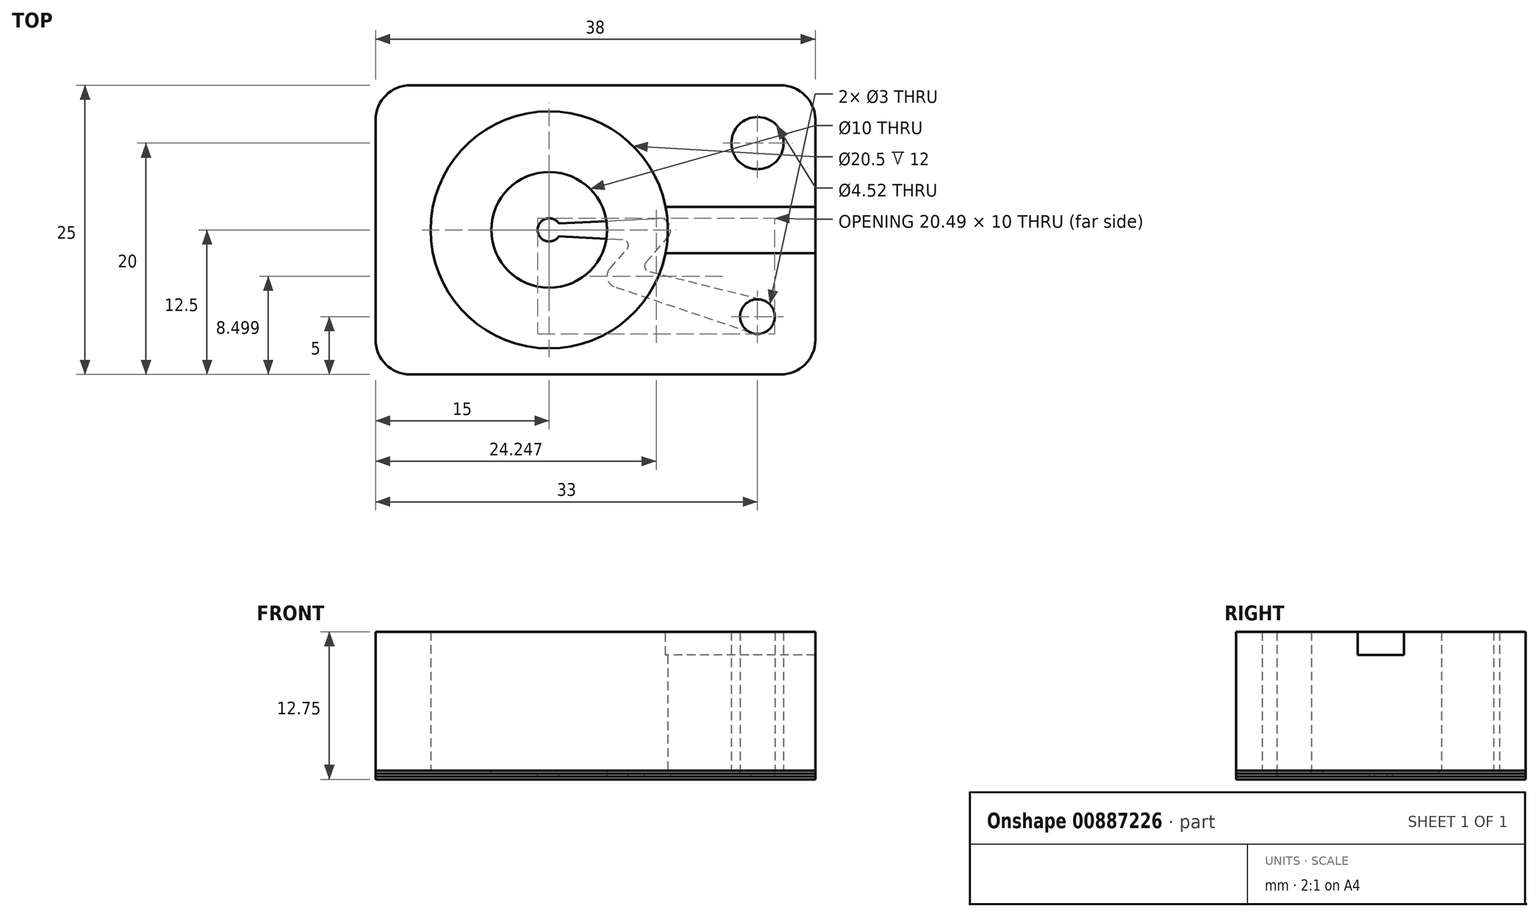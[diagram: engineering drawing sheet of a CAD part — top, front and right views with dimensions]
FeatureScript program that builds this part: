
annotation { "Feature Type Name" : "Feature", "Feature Type Description" : "" }
export const myFeature = defineFeature(function(context is Context, id is Id, definition is map)
    precondition{}
    {
        {
            var Q0;
            Q0=qCreatedBy(makeId("Top.planeOp"),FACE);
            var sketch = newSketch(context, id + "F0", { "sketchPlane" : qUnion([Q0])});
            skLineSegment(sketch, "E0.bottom", {"start": v(16, -12.5) * mm, "end": v(-16, -12.5) * mm});
            skLineSegment(sketch, "E0.top", {"start": v(16, 12.5) * mm, "end": v(-16, 12.5) * mm});
            skLineSegment(sketch, "E0.left", {"start": v(19, -9.5) * mm, "end": v(19, 9.5) * mm});
            skLineSegment(sketch, "E0.right", {"start": v(-19, -9.5) * mm, "end": v(-19, 9.5) * mm});
            skPoint(sketch, "E0.middle", {"position": v(0, 0) * mm});
            skCircle(sketch, "E1", {"center": v(-4, 0) * mm, "radius": 10.25 * mm});
            skLineSegment(sketch, "E2", {"start": v(14, 12.5) * mm, "end": v(14, -12.5) * mm, "construction": true});
            skCircle(sketch, "E3", {"center": v(14, -7.5) * mm, "radius": 1.5 * mm});
            skCircle(sketch, "E4", {"center": v(14, 7.5) * mm, "radius": 2.26 * mm});
            skPoint(sketch, "E5.visualSharp", {"position": v(19, 12.5) * mm});
            skArc(sketch, "E5.filletArc", {"start": v(19, 9.5) * mm, "mid": v(18.12, 11.62) * mm, "end": v(16, 12.5) * mm});
            skPoint(sketch, "E6.visualSharp", {"position": v(-19, 12.5) * mm});
            skArc(sketch, "E6.filletArc", {"start": v(-16, 12.5) * mm, "mid": v(-18.12, 11.62) * mm, "end": v(-19, 9.5) * mm});
            skPoint(sketch, "E7.visualSharp", {"position": v(-19, -12.5) * mm});
            skArc(sketch, "E7.filletArc", {"start": v(-19, -9.5) * mm, "mid": v(-18.12, -11.62) * mm, "end": v(-16, -12.5) * mm});
            skPoint(sketch, "E8.visualSharp", {"position": v(19, -12.5) * mm});
            skArc(sketch, "E8.filletArc", {"start": v(16, -12.5) * mm, "mid": v(18.12, -11.62) * mm, "end": v(19, -9.5) * mm});
            skSolve(sketch);
        }
        {
            var Q0;
            Q0=makeQuery(id+"F0.imprint","IMPRINT",FACE,{"disambiguationData":[TD([[makeQuery(id+"F0.imprint","IMPRINT",EDGE,{"derivedFrom":sQuery(id+"F0.wireOp",EDGE,"E0.bottom")}),-1.0]])]});
            extrude(context, id + "F1", {"entities" : qUnion([Q0]), "depth" : 12 * mm, "offsetDistance" : 25 * mm});
        }
        {
            var Q0;
            Q0=makeQuery(id+"F1.opExtrude","CAP_FACE",FACE,{"disambiguationData":[OSD([sQuery(id+"F0.wireOp",EDGE,"E0.bottom"),sQuery(id+"F0.wireOp",EDGE,"E0.top"),sQuery(id+"F0.wireOp",EDGE,"E0.left"),sQuery(id+"F0.wireOp",EDGE,"E0.right"),sQuery(id+"F0.wireOp",EDGE,"E1"),sQuery(id+"F0.wireOp",EDGE,"E3"),sQuery(id+"F0.wireOp",EDGE,"E4"),sQuery(id+"F0.wireOp",EDGE,"E5.filletArc"),sQuery(id+"F0.wireOp",EDGE,"E6.filletArc"),sQuery(id+"F0.wireOp",EDGE,"E7.filletArc"),sQuery(id+"F0.wireOp",EDGE,"E8.filletArc")])],"isStart":false});
            var sketch = newSketch(context, id + "F2", { "sketchPlane" : qUnion([Q0])});
            skLineSegment(sketch, "E9.0", {"start": v(19, -2) * mm, "end": v(19, 2) * mm});
            skArc(sketch, "E10.0", {"start": v(6.05, -2) * mm, "mid": v(6.25, 0) * mm, "end": v(6.05, 2) * mm});
            skLineSegment(sketch, "E11.bottom", {"start": v(19, -2) * mm, "end": v(6.05, -2) * mm});
            skLineSegment(sketch, "E11.top", {"start": v(19, 2) * mm, "end": v(6.05, 2) * mm});
            skPoint(sketch, "E11.middle", {"position": v(13.13, 0) * mm});
            skPoint(sketch, "E12.orphan", {"position": v(22.63, 2) * mm});
            skPoint(sketch, "E13.orphan", {"position": v(22.63, -2) * mm});
            skPoint(sketch, "E14.orphan", {"position": v(19, -9.5) * mm});
            skPoint(sketch, "E11.right.start.orphan", {"position": v(3.62, -2) * mm});
            skPoint(sketch, "E15.orphan", {"position": v(3.62, 2) * mm});
            skPoint(sketch, "E16.orphan", {"position": v(19, 9.5) * mm});
            skSolve(sketch);
        }
        {
            var Q0;
            Q0=makeQuery(id+"F2.imprint","IMPRINT",FACE,{"disambiguationData":[TD([[makeQuery(id+"F2.imprint","IMPRINT",EDGE,{"derivedFrom":sQuery(id+"F2.wireOp",EDGE,"E9.0")}),1.0]])]});
            extrude(context, id + "F3", {"entities" : qUnion([Q0]), "operationType" : NewBodyOperationType.REMOVE, "oppositeDirection" : true, "depth" : 2 * mm, "offsetDistance" : 25 * mm});
        }
        {
            var Q0;
            Q0=makeQuery(id+"F1.opExtrude","CAP_FACE",FACE,{"disambiguationData":[OSD([sQuery(id+"F0.wireOp",EDGE,"E0.bottom"),sQuery(id+"F0.wireOp",EDGE,"E0.top"),sQuery(id+"F0.wireOp",EDGE,"E0.left"),sQuery(id+"F0.wireOp",EDGE,"E0.right"),sQuery(id+"F0.wireOp",EDGE,"E1"),sQuery(id+"F0.wireOp",EDGE,"E3"),sQuery(id+"F0.wireOp",EDGE,"E4"),sQuery(id+"F0.wireOp",EDGE,"E5.filletArc"),sQuery(id+"F0.wireOp",EDGE,"E6.filletArc"),sQuery(id+"F0.wireOp",EDGE,"E7.filletArc"),sQuery(id+"F0.wireOp",EDGE,"E8.filletArc")])],"isStart":true});
            var sketch = newSketch(context, id + "F4", { "sketchPlane" : qUnion([Q0])});
            skLineSegment(sketch, "E17.0", {"start": v(16, -12.5) * mm, "end": v(-16, -12.5) * mm});
            skArc(sketch, "E18.0", {"start": v(19, -9.5) * mm, "mid": v(18.12, -11.62) * mm, "end": v(16, -12.5) * mm});
            skLineSegment(sketch, "E19.0", {"start": v(19, 9.5) * mm, "end": v(19, -9.5) * mm});
            skArc(sketch, "E20.0", {"start": v(16, 12.5) * mm, "mid": v(18.12, 11.62) * mm, "end": v(19, 9.5) * mm});
            skLineSegment(sketch, "E21.0", {"start": v(16, 12.5) * mm, "end": v(-16, 12.5) * mm});
            skArc(sketch, "E22.0", {"start": v(-19, 9.5) * mm, "mid": v(-18.12, 11.62) * mm, "end": v(-16, 12.5) * mm});
            skLineSegment(sketch, "E23.0", {"start": v(-19, 9.5) * mm, "end": v(-19, -9.5) * mm});
            skArc(sketch, "E24.0", {"start": v(-16, -12.5) * mm, "mid": v(-18.12, -11.62) * mm, "end": v(-19, -9.5) * mm});
            skCircle(sketch, "E25", {"center": v(-4, 0) * mm, "radius": 5 * mm});
            skSolve(sketch);
        }
        {
            var Q0;
            Q0=makeQuery(id+"F4.imprint","IMPRINT",FACE,{"disambiguationData":[TD([[makeQuery(id+"F4.imprint","IMPRINT",EDGE,{"derivedFrom":sQuery(id+"F4.wireOp",EDGE,"E25")}),-1.0]])]});
            var Q1;
            Q1=makeQuery(id+"F4.imprint","IMPRINT",FACE,{"disambiguationData":[TD([[makeQuery(id+"F4.imprint","IMPRINT",EDGE,{"derivedFrom":sQuery(id+"F4.wireOp",EDGE,"E17.0")}),-1.0]])]});
            var Q2;
            Q2=makeQuery(id+"F4.imprint","IMPRINT",FACE,{"disambiguationData":[TD([[makeQuery(id+"F4.imprint","IMPRINT",EDGE,{"derivedFrom":makeQuery(id+"F1.opExtrude","CAP_EDGE",EDGE,{"disambiguationData":[OSD([sQuery(id+"F0.wireOp",EDGE,"E4")])],"isStart":true})}),-1.0]])]});
            extrude(context, id + "F5", {"entities" : qUnion([Q0, Q1, Q2]), "depth" : .25 * mm, "offsetDistance" : 25 * mm});
        }
        {
            var Q0;
            Q0=makeQuery(id+"F5.opExtrude","CAP_FACE",FACE,{"disambiguationData":[OSD([sQuery(id+"F0.wireOp",EDGE,"E3"),sQuery(id+"F4.wireOp",EDGE,"E17.0"),sQuery(id+"F4.wireOp",EDGE,"E18.0"),sQuery(id+"F4.wireOp",EDGE,"E19.0"),sQuery(id+"F4.wireOp",EDGE,"E20.0"),sQuery(id+"F4.wireOp",EDGE,"E21.0"),sQuery(id+"F4.wireOp",EDGE,"E22.0"),sQuery(id+"F4.wireOp",EDGE,"E23.0"),sQuery(id+"F4.wireOp",EDGE,"E24.0"),sQuery(id+"F4.wireOp",EDGE,"E25")])],"isStart":false});
            var sketch = newSketch(context, id + "F6", { "sketchPlane" : qUnion([Q0])});
            skLineSegment(sketch, "E26.0", {"start": v(16, -12.5) * mm, "end": v(-16, -12.5) * mm});
            skArc(sketch, "E27.0", {"start": v(-16, -12.5) * mm, "mid": v(-18.12, -11.62) * mm, "end": v(-19, -9.5) * mm});
            skLineSegment(sketch, "E28.0", {"start": v(-19, 9.5) * mm, "end": v(-19, -9.5) * mm});
            skArc(sketch, "E29.0", {"start": v(-19, 9.5) * mm, "mid": v(-18.12, 11.62) * mm, "end": v(-16, 12.5) * mm});
            skLineSegment(sketch, "E30.0", {"start": v(16, 12.5) * mm, "end": v(-16, 12.5) * mm});
            skArc(sketch, "E31.0", {"start": v(16, 12.5) * mm, "mid": v(18.12, 11.62) * mm, "end": v(19, 9.5) * mm});
            skLineSegment(sketch, "E32.0", {"start": v(19, 9.5) * mm, "end": v(19, -9.5) * mm});
            skArc(sketch, "E33.0", {"start": v(19, -9.5) * mm, "mid": v(18.12, -11.62) * mm, "end": v(16, -12.5) * mm});
            skArc(sketch, "E34.0", {"start": v(14.36, 6.04) * mm, "mid": v(15.42, 7.98) * mm, "end": v(13.41, 8.88) * mm});
            skArc(sketch, "E35", {"start": v(-3.16, 0.54) * mm, "mid": v(-5, 0) * mm, "end": v(-3.16, -0.54) * mm});
            skArc(sketch, "E36", {"start": v(1.68, 4.95) * mm, "mid": v(1.03, 4.26) * mm, "end": v(1.25, 3.34) * mm});
            skArc(sketch, "E37", {"start": v(5.45, -1) * mm, "mid": v(6.4, -0.44) * mm, "end": v(6.25, 0.66) * mm});
            skLineSegment(sketch, "E38", {"start": v(14.36, 6.04) * mm, "end": v(4.63, 3.62) * mm});
            skPoint(sketch, "E39.orphan", {"position": v(14, 9) * mm});
            skLineSegment(sketch, "E40", {"start": v(14.36, 6.04) * mm, "end": v(13.64, 8.96) * mm, "construction": true});
            skLineSegment(sketch, "E41", {"start": v(13.64, 8.96) * mm, "end": v(1.68, 4.95) * mm});
            skLineSegment(sketch, "E42", {"start": v(4.37, 2.8) * mm, "end": v(6.25, 0.66) * mm});
            skLineSegment(sketch, "E43", {"start": v(1.25, 3.34) * mm, "end": v(2.71, 1.66) * mm});
            skLineSegment(sketch, "E44", {"start": v(-3.16, 0.54) * mm, "end": v(2.36, 0.84) * mm});
            skLineSegment(sketch, "E45", {"start": v(-3.16, -0.54) * mm, "end": v(5.45, -1) * mm});
            skPoint(sketch, "E46.orphan", {"position": v(-4, -0.5) * mm});
            skPoint(sketch, "E47.orphan", {"position": v(-4, 0.5) * mm});
            skPoint(sketch, "E48.visualSharp", {"position": v(3.83, 3.43) * mm});
            skArc(sketch, "E48.filletArc", {"start": v(4.63, 3.62) * mm, "mid": v(4.27, 3.29) * mm, "end": v(4.37, 2.8) * mm});
            skPoint(sketch, "E49.visualSharp", {"position": v(3.4, 0.9) * mm});
            skArc(sketch, "E49.filletArc", {"start": v(2.36, 0.84) * mm, "mid": v(2.8, 1.14) * mm, "end": v(2.71, 1.66) * mm});
            skSolve(sketch);
        }
        {
            var Q0;
            Q0=makeQuery(id+"F6.imprint","IMPRINT",FACE,{"disambiguationData":[TD([[makeQuery(id+"F6.imprint","IMPRINT",EDGE,{"derivedFrom":sQuery(id+"F6.wireOp",EDGE,"E26.0")}),-1.0]])]});
            var Q1;
            {var subQ0=sQuery(id+"F6.wireOp",EDGE,"E35");Q1=makeQuery(id+"F6.imprint","IMPRINT",FACE,{"disambiguationData":[TD([[makeQuery(id+"F6.imprint","IMPRINT",EDGE,{"derivedFrom":subQ0}),-1.0]])]});}
            extrude(context, id + "F7", {"entities" : qUnion([Q0, Q1]), "depth" : .25 * mm, "offsetDistance" : 25 * mm});
        }
        {
            var Q0;
            Q0=makeQuery(id+"F7.opExtrude","CAP_FACE",FACE,{"disambiguationData":[OSD([sQuery(id+"F6.wireOp",EDGE,"E26.0"),sQuery(id+"F6.wireOp",EDGE,"E27.0"),sQuery(id+"F6.wireOp",EDGE,"E28.0"),sQuery(id+"F6.wireOp",EDGE,"E29.0"),sQuery(id+"F6.wireOp",EDGE,"E30.0"),sQuery(id+"F6.wireOp",EDGE,"E31.0"),sQuery(id+"F6.wireOp",EDGE,"E32.0"),sQuery(id+"F6.wireOp",EDGE,"E33.0"),sQuery(id+"F6.wireOp",EDGE,"E34.0"),sQuery(id+"F6.wireOp",EDGE,"E35"),sQuery(id+"F6.wireOp",EDGE,"E36"),sQuery(id+"F6.wireOp",EDGE,"E37"),sQuery(id+"F6.wireOp",EDGE,"E38"),sQuery(id+"F6.wireOp",EDGE,"E41"),sQuery(id+"F6.wireOp",EDGE,"E42"),sQuery(id+"F6.wireOp",EDGE,"E43"),sQuery(id+"F6.wireOp",EDGE,"E44"),sQuery(id+"F6.wireOp",EDGE,"E45"),sQuery(id+"F6.wireOp",EDGE,"E48.filletArc"),sQuery(id+"F6.wireOp",EDGE,"E49.filletArc")])],"isStart":false});
            var sketch = newSketch(context, id + "F8", { "sketchPlane" : qUnion([Q0])});
            skLineSegment(sketch, "E50.0", {"start": v(16, -12.5) * mm, "end": v(-16, -12.5) * mm});
            skArc(sketch, "E51.0", {"start": v(-16, -12.5) * mm, "mid": v(-18.12, -11.62) * mm, "end": v(-19, -9.5) * mm});
            skLineSegment(sketch, "E52.0", {"start": v(-19, 9.5) * mm, "end": v(-19, -9.5) * mm});
            skArc(sketch, "E53.0", {"start": v(-19, 9.5) * mm, "mid": v(-18.12, 11.62) * mm, "end": v(-16, 12.5) * mm});
            skLineSegment(sketch, "E54.0", {"start": v(16, 12.5) * mm, "end": v(-16, 12.5) * mm});
            skLineSegment(sketch, "E55.0", {"start": v(19, 9.5) * mm, "end": v(19, -9.5) * mm});
            skArc(sketch, "E56.0", {"start": v(16, 12.5) * mm, "mid": v(18.12, 11.62) * mm, "end": v(19, 9.5) * mm});
            skArc(sketch, "E57.0", {"start": v(19, -9.5) * mm, "mid": v(18.12, -11.62) * mm, "end": v(16, -12.5) * mm});
            skSolve(sketch);
        }
        {
            var Q0;
            Q0=makeQuery(id+"F8.imprint","IMPRINT",FACE,{"disambiguationData":[TD([[makeQuery(id+"F8.imprint","IMPRINT",EDGE,{"derivedFrom":sQuery(id+"F8.wireOp",EDGE,"E50.0")}),-1.0]])]});
            var Q1;
            Q1=makeQuery(id+"F8.imprint","IMPRINT",FACE,{"disambiguationData":[TD([[makeQuery(id+"F8.imprint","IMPRINT",EDGE,{"derivedFrom":makeQuery(id+"F7.opExtrude","CAP_EDGE",EDGE,{"disambiguationData":[OSD([sQuery(id+"F6.wireOp",EDGE,"E34.0")])],"isStart":false})}),-1.0]])]});
            extrude(context, id + "F9", {"entities" : qUnion([Q0, Q1]), "depth" : .25 * mm, "offsetDistance" : 25 * mm});
        }
    });
